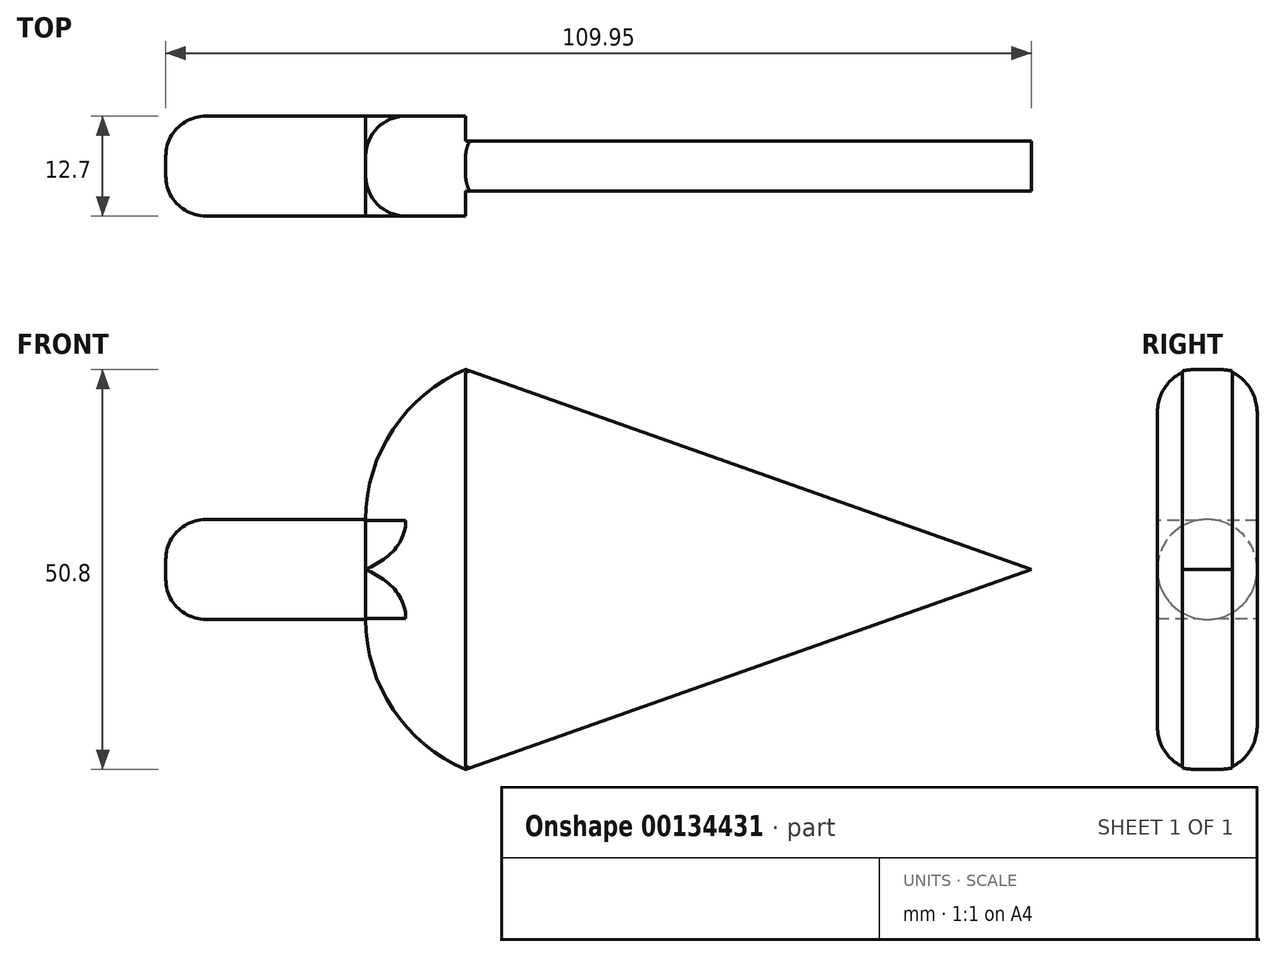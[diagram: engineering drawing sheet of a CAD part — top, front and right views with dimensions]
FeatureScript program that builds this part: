
annotation { "Feature Type Name" : "Feature", "Feature Type Description" : "" }
export const myFeature = defineFeature(function(context is Context, id is Id, definition is map)
    precondition{}
    {
        {
            var Q0;
            Q0=qCreatedBy(makeId("Front.planeOp"),FACE);
            var sketch = newSketch(context, id + "F0", { "sketchPlane" : qUnion([Q0])});
            skLineSegment(sketch, "E0", {"start": v(-43.16, 17.55) * mm, "end": v(-17.76, 17.55) * mm});
            skLineSegment(sketch, "E1", {"start": v(-17.76, 17.55) * mm, "end": v(-17.76, 4.85) * mm});
            skLineSegment(sketch, "E2", {"start": v(-17.76, 4.85) * mm, "end": v(-43.16, 4.85) * mm});
            skLineSegment(sketch, "E3", {"start": v(-43.16, 4.85) * mm, "end": v(-43.16, 17.55) * mm});
            skLineSegment(sketch, "E4", {"start": v(-17.76, 11.2) * mm, "end": v(-5.06, 11.2) * mm});
            skLineSegment(sketch, "E5", {"start": v(-5.06, 11.2) * mm, "end": v(-5.06, 36.6) * mm});
            skLineSegment(sketch, "E6", {"start": v(-5.06, 11.2) * mm, "end": v(-5.06, -14.2) * mm});
            skArc(sketch, "E7", {"start": v(-5.06, 36.6) * mm, "mid": v(-14.3, 29) * mm, "end": v(-17.76, 17.55) * mm});
            skArc(sketch, "E8", {"start": v(-17.76, 4.85) * mm, "mid": v(-14.3, -6.6) * mm, "end": v(-5.06, -14.2) * mm});
            skLineSegment(sketch, "E9", {"start": v(-5.06, -14.2) * mm, "end": v(66.79, 11.2) * mm});
            skLineSegment(sketch, "E10", {"start": v(66.79, 11.2) * mm, "end": v(-5.06, 36.6) * mm});
            skLineSegment(sketch, "E11", {"start": v(-17.76, 11.2) * mm, "end": v(-43.16, 11.2) * mm});
            skSolve(sketch);
        }
        {
            var Q0;
            {var subQ2=sQuery(id+"F0.wireOp",EDGE,"E4");Q0=makeQuery(id+"F0.imprint","IMPRINT",FACE,{"disambiguationData":[TD([[makeQuery(id+"F0.imprint","IMPRINT",EDGE,{"derivedFrom":subQ2}),1.0]])]});}
            var Q1;
            {var subQ2=sQuery(id+"F0.wireOp",EDGE,"E4");Q1=makeQuery(id+"F0.imprint","IMPRINT",FACE,{"disambiguationData":[TD([[makeQuery(id+"F0.imprint","IMPRINT",EDGE,{"derivedFrom":subQ2}),-1.0]])]});}
            extrude(context, id + "F1", {"entities" : qUnion([Q0, Q1]), "endBound" : BoundingType.SYMMETRIC, "depth" : 12.7 * mm});
        }
        {
            var Q0;
            Q0=makeQuery(id+"F0.imprint","IMPRINT",FACE,{"disambiguationData":[TD([[makeQuery(id+"F0.imprint","IMPRINT",EDGE,{"derivedFrom":sQuery(id+"F0.wireOp",EDGE,"E5")}),-1.0]])]});
            extrude(context, id + "F2", {"entities" : qUnion([Q0]), "operationType" : NewBodyOperationType.ADD, "endBound" : BoundingType.SYMMETRIC, "depth" : 6.35 * mm});
        }
        {
            var Q0;
            {var subQ0=sQuery(id+"F0.wireOp",EDGE,"E0");Q0=makeQuery(id+"F0.imprint","IMPRINT",FACE,{"disambiguationData":[TD([[makeQuery(id+"F0.imprint","IMPRINT",EDGE,{"derivedFrom":subQ0}),-1.0]])]});}
            var Q1;
            Q1=sQuery(id+"F0.wireOp",EDGE,"E11");
            revolve(context, id + "F3", {"operationType" : NewBodyOperationType.ADD, "entities" : qUnion([Q0]), "axis" : qUnion([Q1]), "revolveType" : RevolveType.FULL});
        }
        {
            var Q0;
            Q0=makeQuery(id+"F3.opRevolve","SWEPT_EDGE",EDGE,{"disambiguationData":[OSD([sQuery(id+"F0.wireOp",EDGE,"E0"),sQuery(id+"F0.wireOp",EDGE,"E3")])]});
            var Q1;
            Q1=makeQuery(id+"F1.opExtrude","CAP_EDGE",EDGE,{"disambiguationData":[OSD([sQuery(id+"F0.wireOp",EDGE,"E7")])],"isStart":true});
            var Q2;
            Q2=makeQuery(id+"F1.opExtrude","CAP_EDGE",EDGE,{"disambiguationData":[OSD([sQuery(id+"F0.wireOp",EDGE,"E7")])],"isStart":false});
            fillet(context, id + "F4", {"entities" : qUnion([Q0, Q1, Q2]), "radius" : 5.08 * mm, "tangentPropagation" : true, "allowEdgeOverflow" : false});
        }
    });
